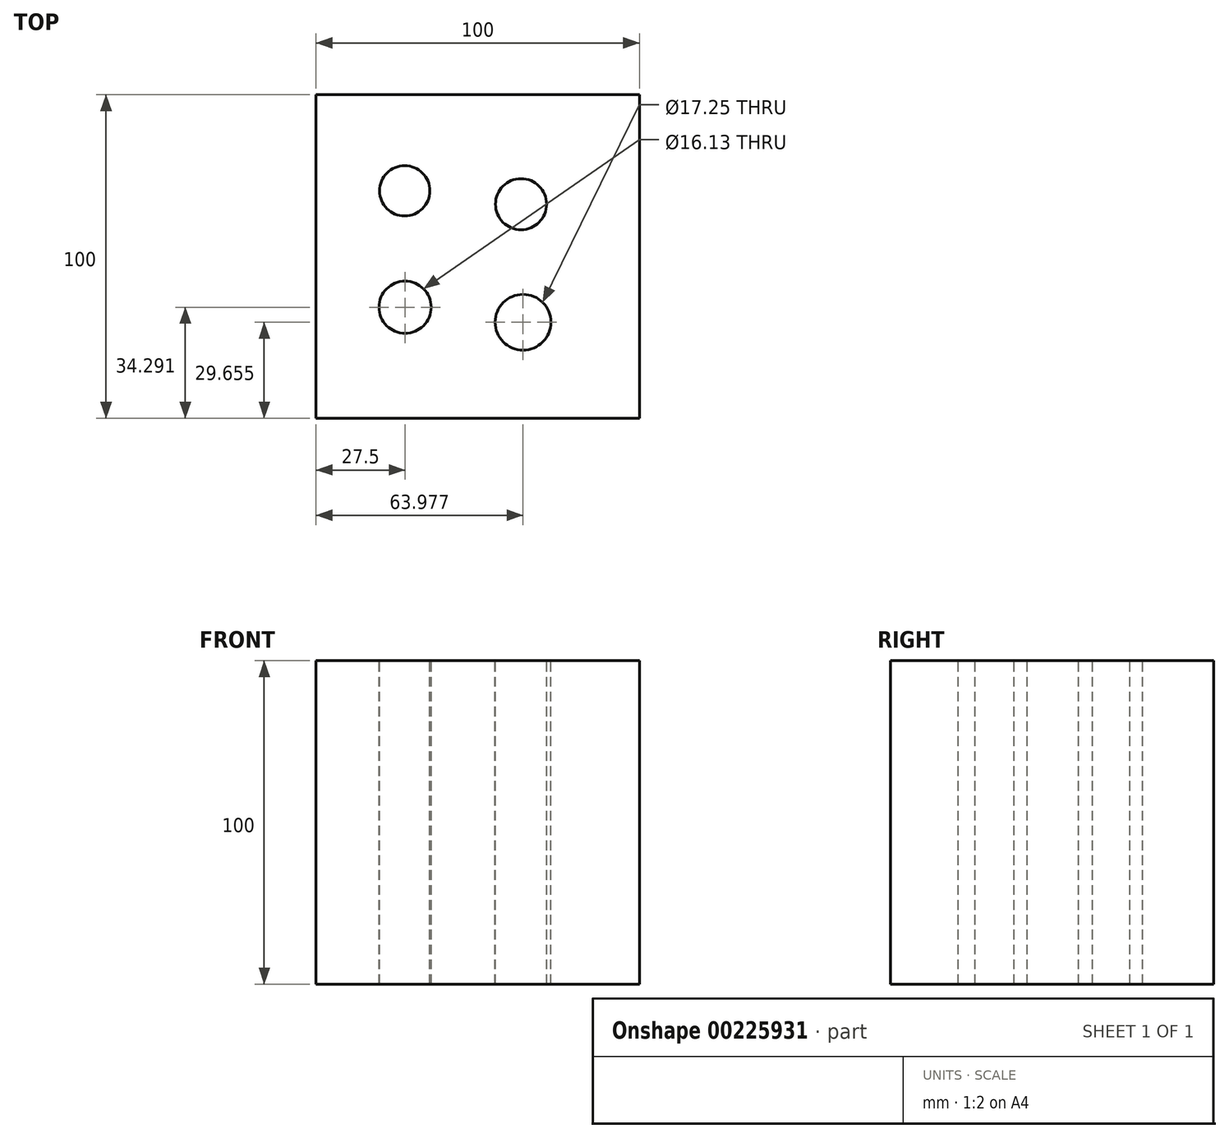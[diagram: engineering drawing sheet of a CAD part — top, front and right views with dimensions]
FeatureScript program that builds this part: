
annotation { "Feature Type Name" : "Feature", "Feature Type Description" : "" }
export const myFeature = defineFeature(function(context is Context, id is Id, definition is map)
    precondition{}
    {
        {
            var Q0;
            Q0=qCreatedBy(makeId("Front.planeOp"),FACE);
            var sketch = newSketch(context, id + "F0", { "sketchPlane" : qUnion([Q0])});
            skLineSegment(sketch, "E0.bottom", {"start": v(0, 0) * mm, "end": v(100, 0) * mm});
            skLineSegment(sketch, "E0.top", {"start": v(0, 100) * mm, "end": v(100, 100) * mm});
            skLineSegment(sketch, "E0.left", {"start": v(0, 0) * mm, "end": v(0, 100) * mm});
            skLineSegment(sketch, "E0.right", {"start": v(100, 0) * mm, "end": v(100, 100) * mm});
            skSolve(sketch);
        }
        {
            var Q0;
            Q0=makeQuery(id+"F0.imprint","IMPRINT",FACE,{"disambiguationData":[TD([[makeQuery(id+"F0.imprint","IMPRINT",EDGE,{"derivedFrom":sQuery(id+"F0.wireOp",EDGE,"E0.bottom")}),1.0]])]});
            extrude(context, id + "F1", {"entities" : qUnion([Q0]), "depth" : 100 * mm});
        }
        {
            var Q0;
            Q0=makeQuery(id+"F1.opExtrude","SWEPT_FACE",FACE,{"disambiguationData":[OSD([sQuery(id+"F0.wireOp",EDGE,"E0.top")])]});
            var sketch = newSketch(context, id + "F2", { "sketchPlane" : qUnion([Q0])});
            skCircle(sketch, "E1", {"center": v(27.4, -29.71) * mm, "radius": 7.78 * mm});
            skCircle(sketch, "E2", {"center": v(63.98, -70.34) * mm, "radius": 8.63 * mm});
            skCircle(sketch, "E3", {"center": v(63.37, -33.85) * mm, "radius": 7.9 * mm});
            skCircle(sketch, "E4", {"center": v(27.5, -65.7) * mm, "radius": 8.06 * mm});
            skSolve(sketch);
        }
        {
            var Q0;
            Q0 = qSketchRegion(id + "F2", true);
            extrude(context, id + "F3", {"entities" : qUnion([Q0]), "operationType" : NewBodyOperationType.REMOVE, "endBound" : BoundingType.THROUGH_ALL, "oppositeDirection" : true, "depth" : 5 * mm});
        }
    });
